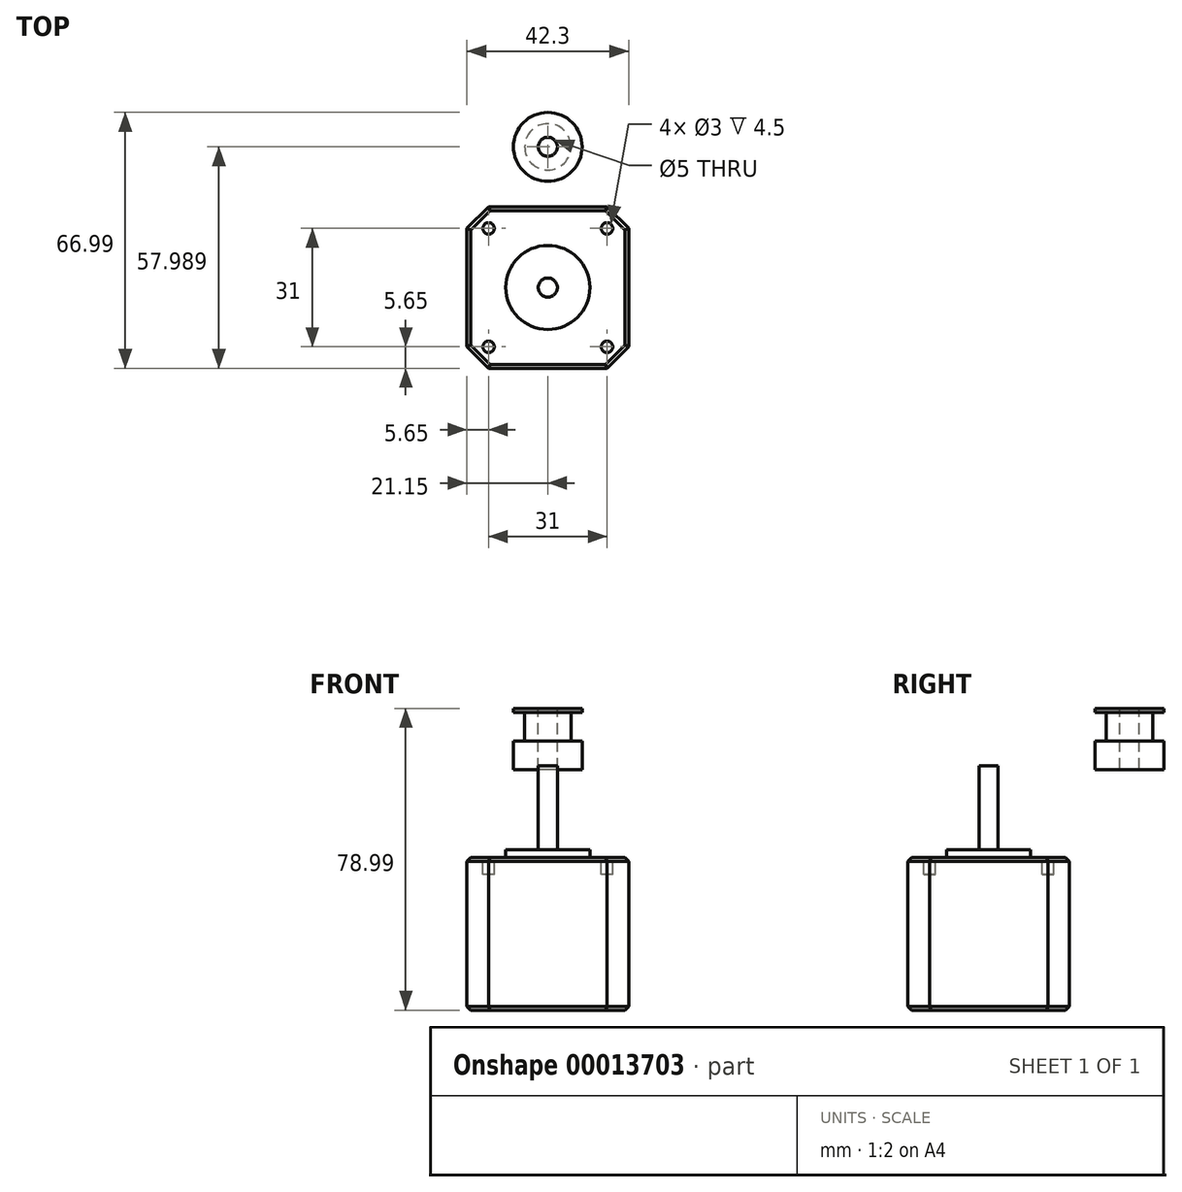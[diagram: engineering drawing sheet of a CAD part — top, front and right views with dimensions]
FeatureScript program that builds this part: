
annotation { "Feature Type Name" : "Feature", "Feature Type Description" : "" }
export const myFeature = defineFeature(function(context is Context, id is Id, definition is map)
    precondition{}
    {
        {
            var Q0;
            Q0=qCreatedBy(makeId("Top.planeOp"),FACE);
            var sketch = newSketch(context, id + "F0", { "sketchPlane" : qUnion([Q0])});
            skLineSegment(sketch, "E0.rect.bottom", {"start": v(21.15, 21.15) * mm, "end": v(-21.15, 21.15) * mm});
            skLineSegment(sketch, "E0.rect.top", {"start": v(21.15, -21.15) * mm, "end": v(-21.15, -21.15) * mm});
            skLineSegment(sketch, "E0.rect.left", {"start": v(21.15, 21.15) * mm, "end": v(21.15, -21.15) * mm});
            skLineSegment(sketch, "E0.rect.right", {"start": v(-21.15, 21.15) * mm, "end": v(-21.15, -21.15) * mm});
            skPoint(sketch, "E0.rect.middle", {"position": v(0, 0) * mm});
            skLineSegment(sketch, "E1.rect.bottom", {"start": v(15.5, 15.5) * mm, "end": v(-15.5, 15.5) * mm, "construction": true});
            skLineSegment(sketch, "E1.rect.top", {"start": v(15.5, -15.5) * mm, "end": v(-15.5, -15.5) * mm, "construction": true});
            skLineSegment(sketch, "E1.rect.left", {"start": v(15.5, 15.5) * mm, "end": v(15.5, -15.5) * mm, "construction": true});
            skLineSegment(sketch, "E1.rect.right", {"start": v(-15.5, 15.5) * mm, "end": v(-15.5, -15.5) * mm, "construction": true});
            skCircle(sketch, "E2", {"center": v(-15.5, 15.5) * mm, "radius": 1.5 * mm});
            skCircle(sketch, "E3", {"center": v(0, 0) * mm, "radius": 11 * mm});
            skCircle(sketch, "E4", {"center": v(15.5, 15.5) * mm, "radius": 1.5 * mm});
            skCircle(sketch, "E5", {"center": v(15.5, -15.5) * mm, "radius": 1.5 * mm});
            skCircle(sketch, "E6", {"center": v(-15.5, -15.5) * mm, "radius": 1.5 * mm});
            skLineSegment(sketch, "E7", {"start": v(15.5, 21.15) * mm, "end": v(21.15, 15.5) * mm});
            skLineSegment(sketch, "E8", {"start": v(21.15, -15.5) * mm, "end": v(15.5, -21.15) * mm});
            skLineSegment(sketch, "E9", {"start": v(-21.15, -15.5) * mm, "end": v(-15.5, -21.15) * mm});
            skLineSegment(sketch, "E10", {"start": v(-21.15, 15.5) * mm, "end": v(-15.5, 21.15) * mm});
            skCircle(sketch, "E11", {"center": v(0, 0) * mm, "radius": 2.5 * mm});
            skSolve(sketch);
        }
        {
            var Q0;
            Q0=makeQuery(id+"F0.imprint","IMPRINT",FACE,{"disambiguationData":[TD([[makeQuery(id+"F0.imprint","IMPRINT",EDGE,{"derivedFrom":sQuery(id+"F0.wireOp",EDGE,"E2")}),-1.0]])]});
            var Q1;
            Q1=makeQuery(id+"F0.imprint","IMPRINT",FACE,{"disambiguationData":[TD([[makeQuery(id+"F0.imprint","IMPRINT",EDGE,{"derivedFrom":sQuery(id+"F0.wireOp",EDGE,"E2")}),1.0]])]});
            var Q2;
            Q2=makeQuery(id+"F0.imprint","IMPRINT",FACE,{"disambiguationData":[TD([[makeQuery(id+"F0.imprint","IMPRINT",EDGE,{"derivedFrom":sQuery(id+"F0.wireOp",EDGE,"E4")}),1.0]])]});
            var Q3;
            Q3=makeQuery(id+"F0.imprint","IMPRINT",FACE,{"disambiguationData":[TD([[makeQuery(id+"F0.imprint","IMPRINT",EDGE,{"derivedFrom":sQuery(id+"F0.wireOp",EDGE,"E5")}),1.0]])]});
            var Q4;
            Q4=makeQuery(id+"F0.imprint","IMPRINT",FACE,{"disambiguationData":[TD([[makeQuery(id+"F0.imprint","IMPRINT",EDGE,{"derivedFrom":sQuery(id+"F0.wireOp",EDGE,"E6")}),1.0]])]});
            var Q5;
            Q5=makeQuery(id+"F0.imprint","IMPRINT",FACE,{"disambiguationData":[TD([[makeQuery(id+"F0.imprint","IMPRINT",EDGE,{"derivedFrom":sQuery(id+"F0.wireOp",EDGE,"E11")}),1.0]])]});
            var Q6;
            Q6=makeQuery(id+"F0.imprint","IMPRINT",FACE,{"disambiguationData":[TD([[makeQuery(id+"F0.imprint","IMPRINT",EDGE,{"derivedFrom":sQuery(id+"F0.wireOp",EDGE,"E3")}),1.0]])]});
            extrude(context, id + "F1", {"entities" : qUnion([Q0, Q1, Q2, Q3, Q4, Q5, Q6]), "oppositeDirection" : true, "depth" : 40 * mm});
        }
        {
            var Q0;
            Q0=makeQuery(id+"F0.imprint","IMPRINT",FACE,{"disambiguationData":[TD([[makeQuery(id+"F0.imprint","IMPRINT",EDGE,{"derivedFrom":sQuery(id+"F0.wireOp",EDGE,"E2")}),1.0]])]});
            var Q1;
            Q1=makeQuery(id+"F0.imprint","IMPRINT",FACE,{"disambiguationData":[TD([[makeQuery(id+"F0.imprint","IMPRINT",EDGE,{"derivedFrom":sQuery(id+"F0.wireOp",EDGE,"E4")}),1.0]])]});
            var Q2;
            Q2=makeQuery(id+"F0.imprint","IMPRINT",FACE,{"disambiguationData":[TD([[makeQuery(id+"F0.imprint","IMPRINT",EDGE,{"derivedFrom":sQuery(id+"F0.wireOp",EDGE,"E5")}),1.0]])]});
            var Q3;
            Q3=makeQuery(id+"F0.imprint","IMPRINT",FACE,{"disambiguationData":[TD([[makeQuery(id+"F0.imprint","IMPRINT",EDGE,{"derivedFrom":sQuery(id+"F0.wireOp",EDGE,"E6")}),1.0]])]});
            extrude(context, id + "F2", {"entities" : qUnion([Q0, Q1, Q2, Q3]), "operationType" : NewBodyOperationType.REMOVE, "oppositeDirection" : true, "depth" : 4.5 * mm});
        }
        {
            var Q0;
            Q0=makeQuery(id+"F0.imprint","IMPRINT",FACE,{"disambiguationData":[TD([[makeQuery(id+"F0.imprint","IMPRINT",EDGE,{"derivedFrom":sQuery(id+"F0.wireOp",EDGE,"E3")}),1.0]])]});
            var Q1;
            Q1=makeQuery(id+"F0.imprint","IMPRINT",FACE,{"disambiguationData":[TD([[makeQuery(id+"F0.imprint","IMPRINT",EDGE,{"derivedFrom":sQuery(id+"F0.wireOp",EDGE,"E11")}),1.0]])]});
            extrude(context, id + "F3", {"entities" : qUnion([Q0, Q1]), "operationType" : NewBodyOperationType.ADD, "depth" : 2 * mm});
        }
        {
            var Q0;
            Q0=makeQuery(id+"F0.imprint","IMPRINT",FACE,{"disambiguationData":[TD([[makeQuery(id+"F0.imprint","IMPRINT",EDGE,{"derivedFrom":sQuery(id+"F0.wireOp",EDGE,"E11")}),1.0]])]});
            extrude(context, id + "F4", {"entities" : qUnion([Q0]), "operationType" : NewBodyOperationType.ADD, "depth" : 24 * mm});
        }
        {
            var Q0;
            Q0=makeQuery(id+"F1.opExtrude","CAP_EDGE",EDGE,{"disambiguationData":[OSD([sQuery(id+"F0.wireOp",EDGE,"E0.rect.bottom")])],"isStart":true});
            var Q1;
            Q1=makeQuery(id+"F1.opExtrude","CAP_EDGE",EDGE,{"disambiguationData":[OSD([sQuery(id+"F0.wireOp",EDGE,"E0.rect.left")])],"isStart":true});
            var Q2;
            Q2=makeQuery(id+"F1.opExtrude","CAP_EDGE",EDGE,{"disambiguationData":[OSD([sQuery(id+"F0.wireOp",EDGE,"E7")])],"isStart":true});
            var Q3;
            Q3=makeQuery(id+"F1.opExtrude","CAP_EDGE",EDGE,{"disambiguationData":[OSD([sQuery(id+"F0.wireOp",EDGE,"E8")])],"isStart":true});
            var Q4;
            Q4=makeQuery(id+"F1.opExtrude","CAP_EDGE",EDGE,{"disambiguationData":[OSD([sQuery(id+"F0.wireOp",EDGE,"E0.rect.top")])],"isStart":true});
            var Q5;
            Q5=makeQuery(id+"F1.opExtrude","CAP_EDGE",EDGE,{"disambiguationData":[OSD([sQuery(id+"F0.wireOp",EDGE,"E9")])],"isStart":true});
            var Q6;
            Q6=makeQuery(id+"F1.opExtrude","CAP_EDGE",EDGE,{"disambiguationData":[OSD([sQuery(id+"F0.wireOp",EDGE,"E0.rect.right")])],"isStart":true});
            var Q7;
            Q7=makeQuery(id+"F1.opExtrude","CAP_EDGE",EDGE,{"disambiguationData":[OSD([sQuery(id+"F0.wireOp",EDGE,"E10")])],"isStart":true});
            var Q8;
            Q8=makeQuery(id+"F1.opExtrude","CAP_EDGE",EDGE,{"disambiguationData":[OSD([sQuery(id+"F0.wireOp",EDGE,"E7")])],"isStart":false});
            var Q9;
            Q9=makeQuery(id+"F1.opExtrude","CAP_EDGE",EDGE,{"disambiguationData":[OSD([sQuery(id+"F0.wireOp",EDGE,"E0.rect.bottom")])],"isStart":false});
            var Q10;
            Q10=makeQuery(id+"F1.opExtrude","CAP_EDGE",EDGE,{"disambiguationData":[OSD([sQuery(id+"F0.wireOp",EDGE,"E10")])],"isStart":false});
            var Q11;
            Q11=makeQuery(id+"F1.opExtrude","CAP_EDGE",EDGE,{"disambiguationData":[OSD([sQuery(id+"F0.wireOp",EDGE,"E0.rect.right")])],"isStart":false});
            var Q12;
            Q12=makeQuery(id+"F1.opExtrude","CAP_EDGE",EDGE,{"disambiguationData":[OSD([sQuery(id+"F0.wireOp",EDGE,"E9")])],"isStart":false});
            var Q13;
            Q13=makeQuery(id+"F1.opExtrude","CAP_EDGE",EDGE,{"disambiguationData":[OSD([sQuery(id+"F0.wireOp",EDGE,"E0.rect.top")])],"isStart":false});
            var Q14;
            Q14=makeQuery(id+"F1.opExtrude","CAP_EDGE",EDGE,{"disambiguationData":[OSD([sQuery(id+"F0.wireOp",EDGE,"E8")])],"isStart":false});
            var Q15;
            Q15=makeQuery(id+"F1.opExtrude","CAP_EDGE",EDGE,{"disambiguationData":[OSD([sQuery(id+"F0.wireOp",EDGE,"E0.rect.left")])],"isStart":false});
            chamfer(context, id + "F5", {"entities" : qUnion([Q0, Q1, Q2, Q3, Q4, Q5, Q6, Q7, Q8, Q9, Q10, Q11, Q12, Q13, Q14, Q15]), "width" : 1 * mm, "tangentPropagation" : true});
        }
        {
            var Q0;
            Q0=qCreatedBy(makeId("Right.planeOp"),FACE);
            var sketch = newSketch(context, id + "F6", { "sketchPlane" : qUnion([Q0])});
            skLineSegment(sketch, "E12", {"start": v(27.84, 23) * mm, "end": v(36.84, 23) * mm});
            skLineSegment(sketch, "E13", {"start": v(27.84, 23) * mm, "end": v(27.84, 30.5) * mm});
            skLineSegment(sketch, "E14", {"start": v(30.8, 30.5) * mm, "end": v(27.84, 30.5) * mm});
            skLineSegment(sketch, "E15", {"start": v(30.8, 30.5) * mm, "end": v(30.8, 38) * mm});
            skLineSegment(sketch, "E16", {"start": v(27.84, 38) * mm, "end": v(30.8, 38) * mm});
            skLineSegment(sketch, "E17", {"start": v(27.84, 38) * mm, "end": v(27.84, 39) * mm});
            skLineSegment(sketch, "E18", {"start": v(36.84, 39) * mm, "end": v(27.84, 39) * mm});
            skLineSegment(sketch, "E19", {"start": v(36.84, 39) * mm, "end": v(36.84, 23) * mm, "construction": true});
            skLineSegment(sketch, "E20", {"start": v(34.34, 23) * mm, "end": v(34.34, 39) * mm});
            skSolve(sketch);
        }
        {
            var Q0;
            {var subQ3=sQuery(id+"F6.wireOp",EDGE,"E13");Q0=makeQuery(id+"F6.imprint","IMPRINT",FACE,{"disambiguationData":[TD([[makeQuery(id+"F6.imprint","IMPRINT",EDGE,{"derivedFrom":subQ3}),-1.0]])]});}
            var Q1;
            Q1=sQuery(id+"F6.wireOp",EDGE,"E19");
            revolve(context, id + "F7", {"entities" : qUnion([Q0]), "axis" : qUnion([Q1]), "revolveType" : RevolveType.FULL});
        }
    });
